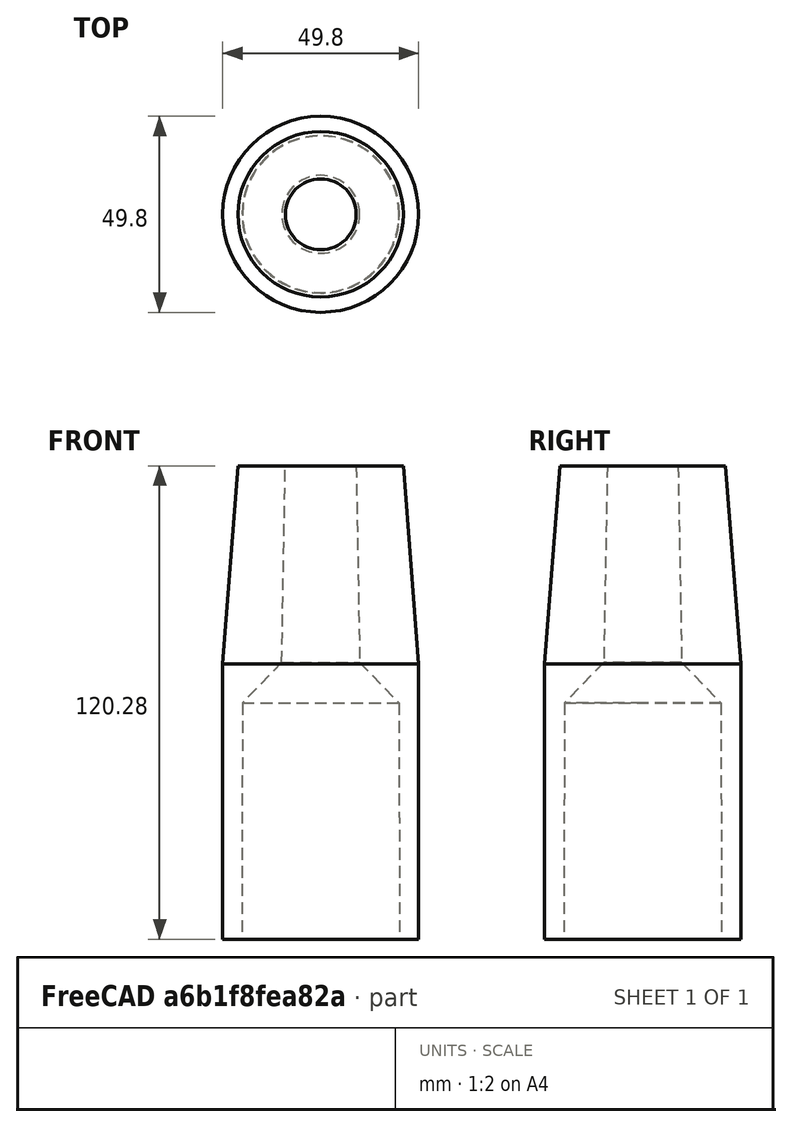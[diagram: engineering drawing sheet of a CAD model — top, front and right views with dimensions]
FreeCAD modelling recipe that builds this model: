
FCSTD DOCUMENT  (FreeCAD 0.14R3700 (Git))
Label: Tube aspirateur
License: CC-BY 3.0
LicenseURL: http://creativecommons.org/licenses/by/3.0/
objects: Sketcher::SketchObject×1, PartDesign::Revolution×1
note: 3 computed .brp shape members not serialized (recipe doc carries the construction recipe); baked Part::Feature solids carry a one-line shape summary decoded from their .brp

FEATURE [Sketcher::SketchObject] Sketch
  Placement = pos=(0,0,0) rot=(-1,0,0;4.71239rad)
  sketch-geometry (7):
    g0: LineSegment StartX=-24.9 StartY=34.11 StartZ=0 EndX=-21 EndY=84.3892 EndZ=0
    g1: LineSegment StartX=-9.9 StartY=34.3892 StartZ=0 EndX=-9 EndY=84.3892 EndZ=0
    g2: LineSegment StartX=-21 StartY=84.3892 StartZ=0 EndX=-9 EndY=84.3892 EndZ=0
    g3: LineSegment StartX=-24.9 StartY=34.11 StartZ=0 EndX=-24.9 EndY=-35.89 EndZ=0
    g4: LineSegment StartX=-9.9 StartY=34.3892 StartZ=0 EndX=-19.9 EndY=24.11 EndZ=0
    g5: LineSegment StartX=-19.9 StartY=24.11 StartZ=0 EndX=-20 EndY=-35.89 EndZ=0
    g6: LineSegment StartX=-24.9 StartY=-35.89 StartZ=0 EndX=-20 EndY=-35.89 EndZ=0
  constraints (19):
    c: Coincident(g2,g0)
    c: Horizontal(g2)
    c: Coincident(g1,g2)
    c: DistanceX(g2) = 12
    c: DistanceY(g1,g1) = -50
    c: Vertical(g3)
    c: DistanceY(g3) = -70
    c: Coincident(g5,g4)
    c: DistanceY(g4,g0) = 10
    c: DistanceX(g0,g1) = 15
    c: DistanceX(g3,g5) = 4.9
    c: Coincident(g3,g0)
    c: Coincident(g4,g1)
    c: Coincident(g6,g3)
    c: Coincident(g6,g5)
    c: Horizontal(g6)
    c: DistanceX(g-1,g5) = -20
    c: DistanceX(g3,g4) = 5
    c: DistanceX(g-1,g1) = -9
FEATURE [PartDesign::Revolution] Revolution
  Angle = 360
  Axis = (0,0,1)
  Base = (0,0,0)
  Placement = pos=(0,0,0) rot=(-1,0,0;4.71239rad)
  ReferenceAxis = -> Sketch [V_Axis]
  Sketch = -> Sketch
